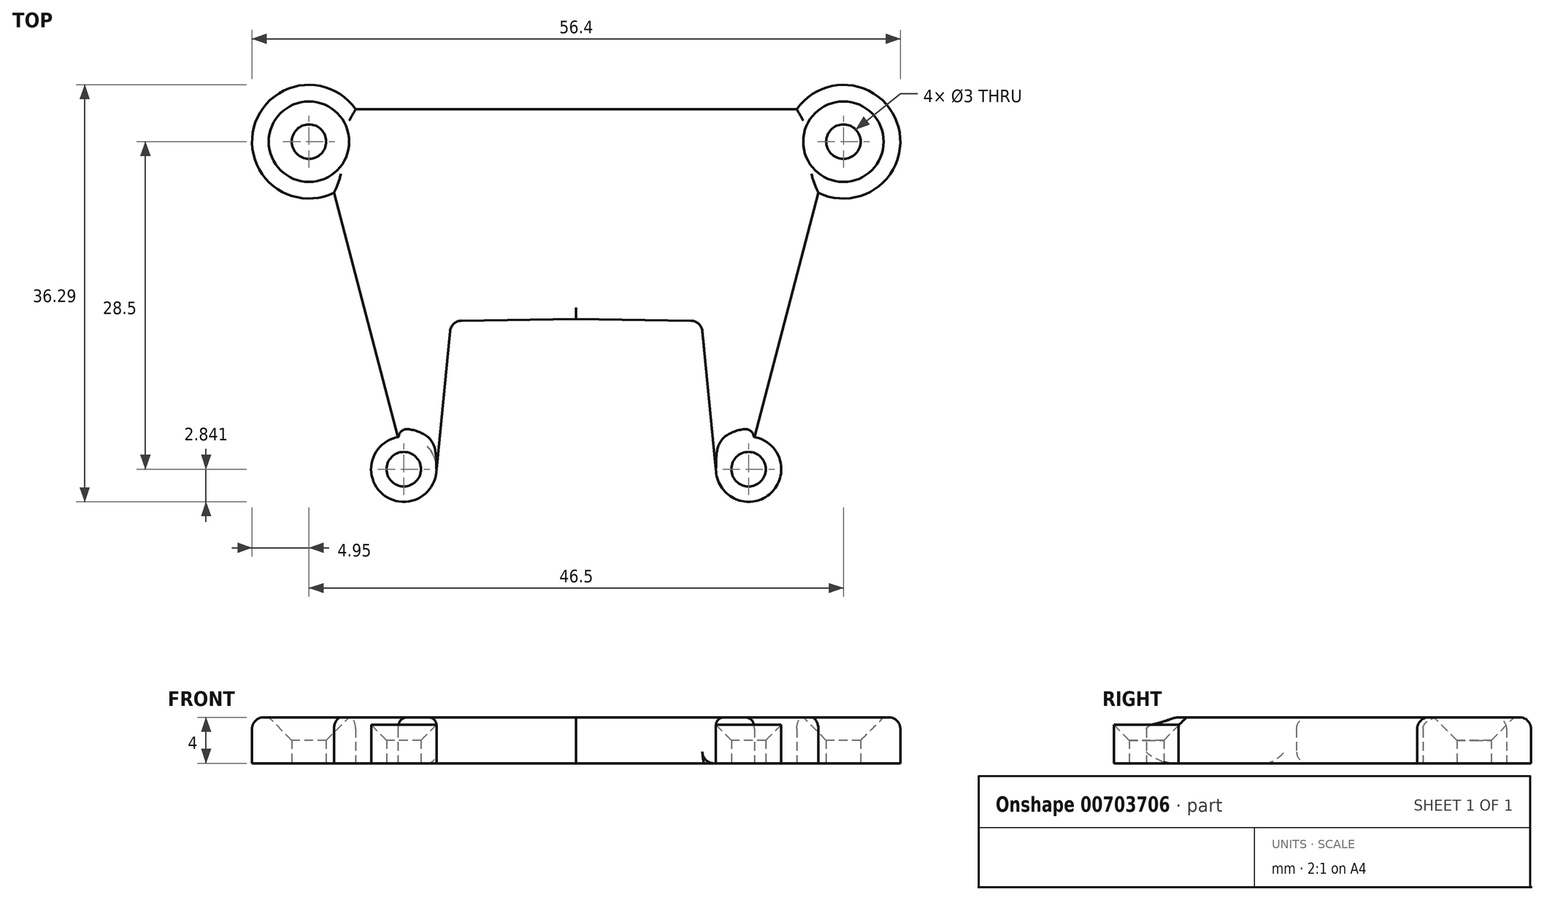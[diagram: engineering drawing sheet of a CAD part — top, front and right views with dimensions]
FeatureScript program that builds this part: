
annotation { "Feature Type Name" : "Feature", "Feature Type Description" : "" }
export const myFeature = defineFeature(function(context is Context, id is Id, definition is map)
    precondition{}
    {
        {
            var Q0;
            Q0=qCreatedBy(makeId("Top.planeOp"),FACE);
            var sketch = newSketch(context, id + "F0", { "sketchPlane" : qUnion([Q0])});
            skCircle(sketch, "E0", {"center": v(-23.25, 13.6) * mm, "radius": 1.5 * mm});
            skCircle(sketch, "E1", {"center": v(-15, -14.9) * mm, "radius": 1.5 * mm});
            skLineSegment(sketch, "E2", {"start": v(-19.2, 16.43) * mm, "end": v(0, 16.43) * mm});
            skLineSegment(sketch, "E3", {"start": v(-21.07, 9.16) * mm, "end": v(-15.5, -12.1) * mm});
            skLineSegment(sketch, "E4", {"start": v(-12.16, -14.9) * mm, "end": v(-10.97, -2.89) * mm});
            skArc(sketch, "E5", {"start": v(-10.97, -2.89) * mm, "mid": v(-10.65, -2.25) * mm, "end": v(-9.99, -1.98) * mm});
            skLineSegment(sketch, "E6", {"start": v(-9.99, -1.98) * mm, "end": v(0, -1.85) * mm});
            skArc(sketch, "E7", {"start": v(-15.5, -12.1) * mm, "mid": v(-16.82, -17.08) * mm, "end": v(-12.16, -14.9) * mm});
            skArc(sketch, "E8", {"start": v(-19.2, 16.43) * mm, "mid": v(-28.04, 14.83) * mm, "end": v(-21.07, 9.16) * mm});
            skLineSegment(sketch, "E9.MirrorCS", {"start": v(19.2, 16.43) * mm, "end": v(0, 16.43) * mm});
            skArc(sketch, "E10.MirrorCS", {"start": v(19.2, 16.43) * mm, "mid": v(28.04, 14.83) * mm, "end": v(21.07, 9.16) * mm});
            skCircle(sketch, "E11.MirrorC", {"center": v(23.25, 13.6) * mm, "radius": 1.5 * mm});
            skLineSegment(sketch, "E12.MirrorCS", {"start": v(21.07, 9.16) * mm, "end": v(15.5, -12.1) * mm});
            skArc(sketch, "E13.MirrorCS", {"start": v(15.5, -12.1) * mm, "mid": v(16.82, -17.08) * mm, "end": v(12.16, -14.9) * mm});
            skLineSegment(sketch, "E14.MirrorCS", {"start": v(12.16, -14.9) * mm, "end": v(10.97, -2.89) * mm});
            skArc(sketch, "E15.MirrorCS", {"start": v(10.97, -2.89) * mm, "mid": v(10.65, -2.25) * mm, "end": v(9.99, -1.98) * mm});
            skLineSegment(sketch, "E16.MirrorCS", {"start": v(9.99, -1.98) * mm, "end": v(0, -1.85) * mm});
            skCircle(sketch, "E17.MirrorC", {"center": v(15, -14.9) * mm, "radius": 1.5 * mm});
            skSolve(sketch);
        }
        {
            var Q0;
            Q0 = qSketchRegion(id + "F0", true);
            extrude(context, id + "F1", {"entities" : qUnion([Q0]), "depth" : 4 * mm, "offsetDistance" : 25 * mm});
        }
        {
            var Q0;
            Q0=makeQuery(id+"F1.opExtrude","CAP_EDGE",EDGE,{"disambiguationData":[OSD([sQuery(id+"F0.wireOp",EDGE,"E0")])],"isStart":false});
            var Q1;
            Q1=makeQuery(id+"F1.opExtrude","CAP_EDGE",EDGE,{"disambiguationData":[OSD([sQuery(id+"F0.wireOp",EDGE,"E11.MirrorC")])],"isStart":false});
            var Q2;
            Q2=makeQuery(id+"F1.opExtrude","CAP_EDGE",EDGE,{"disambiguationData":[OSD([sQuery(id+"F0.wireOp",EDGE,"E1")])],"isStart":false});
            var Q3;
            Q3=makeQuery(id+"F1.opExtrude","CAP_EDGE",EDGE,{"disambiguationData":[OSD([sQuery(id+"F0.wireOp",EDGE,"E17.MirrorC")])],"isStart":false});
            chamfer(context, id + "F2", {"entities" : qUnion([Q0, Q1, Q2, Q3]), "width" : 2 * mm, "tangentPropagation" : true});
        }
        {
            var Q0;
            Q0=makeQuery(id+"F1.opExtrude","CAP_EDGE",EDGE,{"disambiguationData":[OSD([sQuery(id+"F0.wireOp",EDGE,"E2"),sQuery(id+"F0.wireOp",EDGE,"E9.MirrorCS")])],"isStart":false});
            var Q1;
            Q1=makeQuery(id+"F1.opExtrude","CAP_EDGE",EDGE,{"disambiguationData":[OSD([sQuery(id+"F0.wireOp",EDGE,"E8")])],"isStart":false});
            var Q2;
            Q2=makeQuery(id+"F1.opExtrude","CAP_EDGE",EDGE,{"disambiguationData":[OSD([sQuery(id+"F0.wireOp",EDGE,"E3")])],"isStart":false});
            var Q3;
            Q3=makeQuery(id+"F1.opExtrude","CAP_EDGE",EDGE,{"disambiguationData":[OSD([sQuery(id+"F0.wireOp",EDGE,"E4")])],"isStart":true});
            var Q4;
            Q4=makeQuery(id+"F1.opExtrude","CAP_EDGE",EDGE,{"disambiguationData":[OSD([sQuery(id+"F0.wireOp",EDGE,"E5")])],"isStart":false});
            var Q5;
            Q5=makeQuery(id+"F1.opExtrude","CAP_EDGE",EDGE,{"disambiguationData":[OSD([sQuery(id+"F0.wireOp",EDGE,"E6")])],"isStart":false});
            var Q6;
            Q6=makeQuery(id+"F1.opExtrude","CAP_EDGE",EDGE,{"disambiguationData":[OSD([sQuery(id+"F0.wireOp",EDGE,"E14.MirrorCS")])],"isStart":false});
            var Q7;
            Q7=makeQuery(id+"F1.opExtrude","CAP_EDGE",EDGE,{"disambiguationData":[OSD([sQuery(id+"F0.wireOp",EDGE,"E12.MirrorCS")])],"isStart":false});
            var Q8;
            Q8=makeQuery(id+"F1.opExtrude","CAP_EDGE",EDGE,{"disambiguationData":[OSD([sQuery(id+"F0.wireOp",EDGE,"E10.MirrorCS")])],"isStart":false});
            fillet(context, id + "F3", {"entities" : qUnion([Q0, Q1, Q2, Q3, Q4, Q5, Q6, Q7, Q8]), "radius" : 1 * mm, "tangentPropagation" : true, "allowEdgeOverflow" : false});
        }
    });
